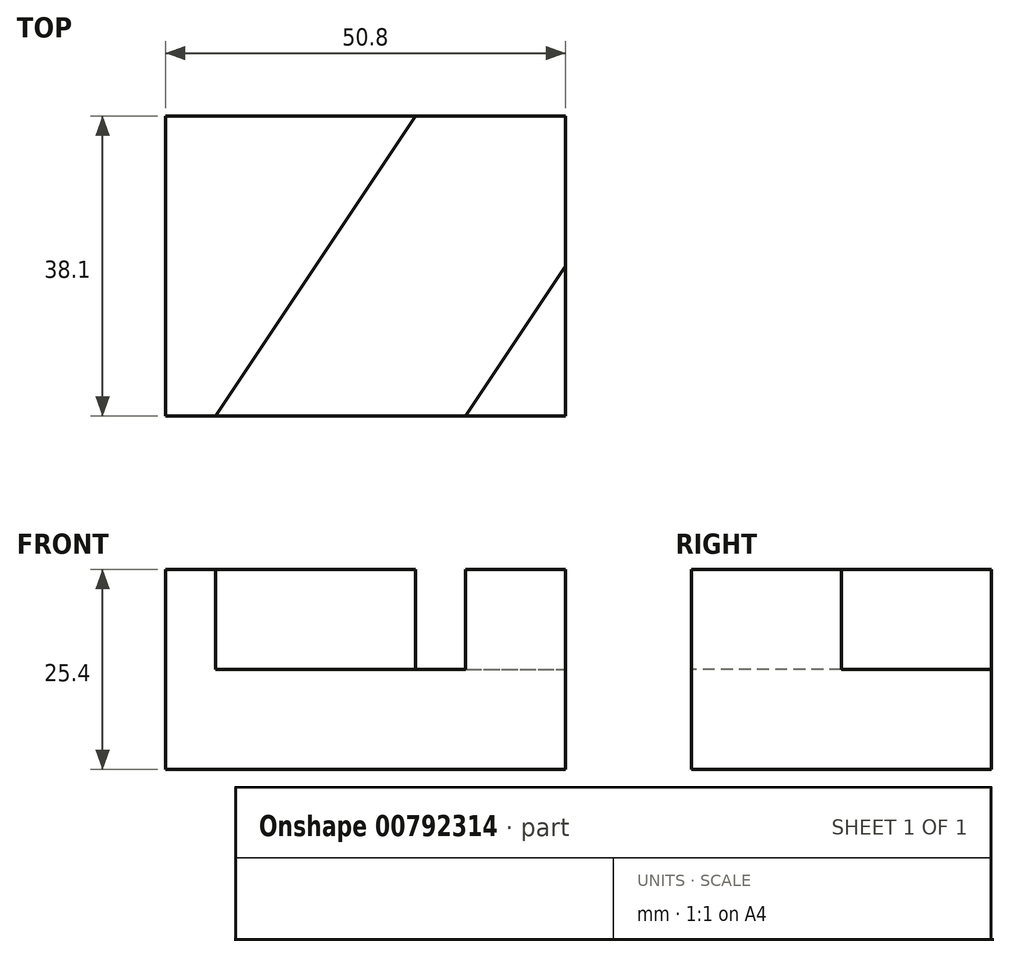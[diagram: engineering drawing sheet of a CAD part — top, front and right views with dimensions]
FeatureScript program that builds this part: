
annotation { "Feature Type Name" : "Feature", "Feature Type Description" : "" }
export const myFeature = defineFeature(function(context is Context, id is Id, definition is map)
    precondition{}
    {
        {
            var Q0;
            Q0=qCreatedBy(makeId("Top.planeOp"),FACE);
            var sketch = newSketch(context, id + "F0", { "sketchPlane" : qUnion([Q0])});
            skLineSegment(sketch, "E0.bottom", {"start": v(0, 0) * mm, "end": v(50.8, 0) * mm});
            skLineSegment(sketch, "E0.top", {"start": v(0, 38.1) * mm, "end": v(50.8, 38.1) * mm});
            skLineSegment(sketch, "E0.left", {"start": v(0, 0) * mm, "end": v(0, 38.1) * mm});
            skLineSegment(sketch, "E0.right", {"start": v(50.8, 0) * mm, "end": v(50.8, 38.1) * mm});
            skSolve(sketch);
        }
        {
            var Q0;
            Q0=qSketchRegion(id+"F0",true);
            extrude(context, id + "F1", {"entities" : qUnion([Q0]), "depth" : 25.4 * mm, "offsetDistance" : 25.4 * mm});
        }
        {
            var Q0;
            Q0=makeQuery(id+"F1.opExtrude","CAP_FACE",FACE,{"disambiguationData":[OSD([sQuery(id+"F0.wireOp",EDGE,"E0.bottom"),sQuery(id+"F0.wireOp",EDGE,"E0.top"),sQuery(id+"F0.wireOp",EDGE,"E0.left"),sQuery(id+"F0.wireOp",EDGE,"E0.right")])],"isStart":false});
            var sketch = newSketch(context, id + "F2", { "sketchPlane" : qUnion([Q0])});
            skLineSegment(sketch, "E1", {"start": v(0, 0) * mm, "end": v(6.35, 0) * mm});
            skLineSegment(sketch, "E2", {"start": v(50.8, 38.1) * mm, "end": v(31.75, 38.1) * mm});
            skLineSegment(sketch, "E3", {"start": v(50.8, 0) * mm, "end": v(38.1, 0) * mm});
            skLineSegment(sketch, "E4", {"start": v(50.8, 0) * mm, "end": v(50.8, 19.05) * mm});
            skLineSegment(sketch, "E5", {"start": v(31.75, 38.1) * mm, "end": v(6.35, 0) * mm});
            skLineSegment(sketch, "E6", {"start": v(38.1, 0) * mm, "end": v(50.8, 19.05) * mm});
            skSolve(sketch);
        }
        {
            var Q0;
            {var subQ3=sQuery(id+"F2.wireOp",EDGE,"E2");Q0=makeQuery(id+"F2.imprint","IMPRINT",FACE,{"disambiguationData":[TD([[makeQuery(id+"F2.imprint","IMPRINT",EDGE,{"derivedFrom":subQ3}),-1.0]])]});}
            extrude(context, id + "F3", {"entities" : qUnion([Q0]), "operationType" : NewBodyOperationType.REMOVE, "oppositeDirection" : true, "depth" : 12.7 * mm, "offsetDistance" : 25.4 * mm});
        }
    });
